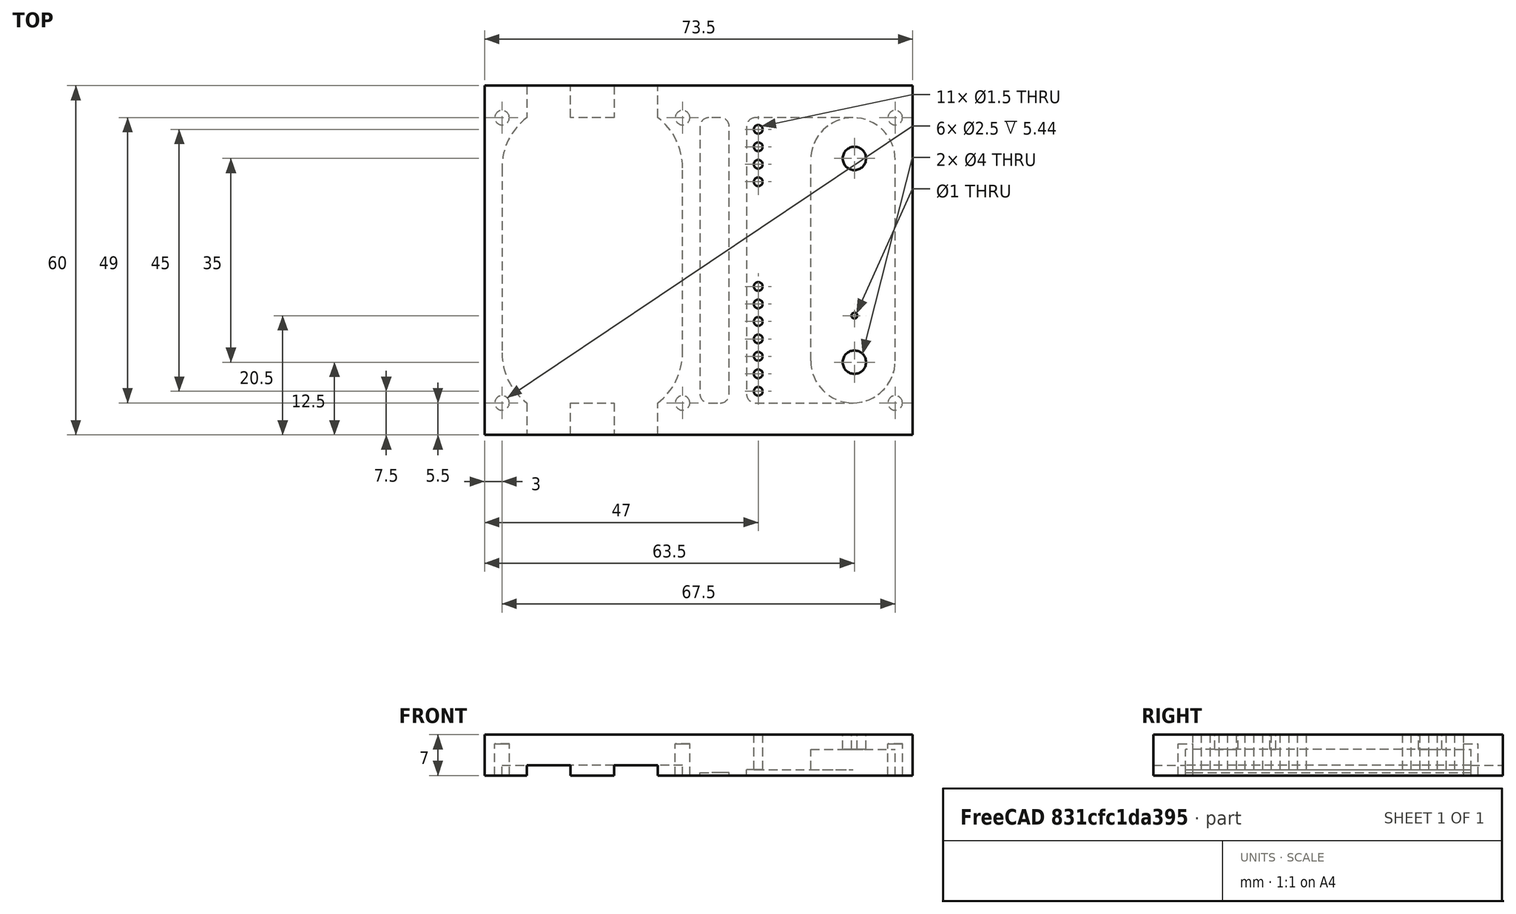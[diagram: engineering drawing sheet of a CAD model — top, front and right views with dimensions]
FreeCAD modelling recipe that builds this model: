
FCSTD DOCUMENT  (FreeCAD 0.20R29177 +426 (Git))
Label: TopCover_2D_TextLaserEngraving
License: All rights reserved
LicenseURL: http://en.wikipedia.org/wiki/All_rights_reserved
objects: Part::Part2DObjectPython×37, Part::Feature×1, App::DocumentObjectGroup×1, App::Part×1
note: 38 computed .brp shape members not serialized (recipe doc carries the construction recipe); baked Part::Feature solids carry a one-line shape summary decoded from their .brp

FEATURE [Part::Feature] Part__Feature001  label="TopCover3D"
  Placement = pos=(0,0,-7.01) rot=(0.707107,-0.707107,0;3.14159rad)
  shape: bbox 73.5 x 60 x 7 mm, 72 faces (baked)
FEATURE [Part::Part2DObjectPython] Shape2DView  label="TopCover_2D"  # Draft 2D object (typed FeaturePython)
  AutoUpdate = true
  Clip = false
  FaceNumbers = [71]
  FuseArch = false
  HiddenLines = false
  InPlace = true
  OnlySolids = false
  Projection = (0,8.74228e-08,-1)
  ProjectionMode = 0
  SegmentLength = 0.05
  Tessellation = false
  VisibleOnly = false
FEATURE [Part::Part2DObjectPython] ShapeString  label="POWER"  # Draft 2D object (typed FeaturePython)
  FontFile = <path>
  MakeFace = true
  Placement = pos=(-25.5,-50.85,0) rot=(0,0,1;0rad)
  Size = 2
  String = POWER
  Tracking = 0
  expr: String = Label
FEATURE [Part::Part2DObjectPython] Shape2DView001  # Draft 2D object (typed FeaturePython)
  AutoUpdate = true
  Base = -> ShapeString
  Clip = false
  FuseArch = false
  HiddenLines = false
  InPlace = true
  OnlySolids = false
  Projection = (0,0,1)
  ProjectionMode = 0
  SegmentLength = 0.05
  Tessellation = false
  VisibleOnly = false
FEATURE [Part::Part2DObjectPython] ShapeString001  label="READY"  # Draft 2D object (typed FeaturePython)
  FontFile = <path>
  MakeFace = true
  Placement = pos=(-25.5,-47.85,0) rot=(0,0,1;0rad)
  Size = 2
  String = READY
  Tracking = 0
  expr: String = Label
FEATURE [Part::Part2DObjectPython] Shape2DView002  # Draft 2D object (typed FeaturePython)
  AutoUpdate = true
  Base = -> ShapeString001
  Clip = false
  FuseArch = false
  HiddenLines = false
  InPlace = true
  OnlySolids = false
  Projection = (0,0,1)
  ProjectionMode = 0
  SegmentLength = 0.05
  Tessellation = false
  VisibleOnly = false
FEATURE [Part::Part2DObjectPython] ShapeString002  label="WAIT"  # Draft 2D object (typed FeaturePython)
  FontFile = <path>
  MakeFace = true
  Placement = pos=(-25.3,-44.85,0) rot=(0,0,1;0rad)
  Size = 2
  String = WAIT
  Tracking = 0
  expr: String = Label
FEATURE [Part::Part2DObjectPython] Shape2DView003  # Draft 2D object (typed FeaturePython)
  AutoUpdate = true
  Base = -> ShapeString002
  Clip = false
  FuseArch = false
  HiddenLines = false
  InPlace = true
  OnlySolids = false
  Projection = (0,0,1)
  ProjectionMode = 0
  SegmentLength = 0.05
  Tessellation = false
  VisibleOnly = false
FEATURE [Part::Part2DObjectPython] ShapeString003  label="PORT1"  # Draft 2D object (typed FeaturePython)
  FontFile = <path>
  MakeFace = true
  Placement = pos=(-25.5,-41.85,0) rot=(0,0,1;0rad)
  Size = 2
  String = PORT1
  Tracking = 0
  expr: String = Label
FEATURE [Part::Part2DObjectPython] Shape2DView004  # Draft 2D object (typed FeaturePython)
  AutoUpdate = true
  Base = -> ShapeString003
  Clip = false
  FuseArch = false
  HiddenLines = false
  InPlace = true
  OnlySolids = false
  Projection = (0,0,1)
  ProjectionMode = 0
  SegmentLength = 0.05
  Tessellation = false
  VisibleOnly = false
FEATURE [Part::Part2DObjectPython] ShapeString004  label="PORT2"  # Draft 2D object (typed FeaturePython)
  FontFile = <path>
  MakeFace = true
  Placement = pos=(-25.5,-38.85,0) rot=(0,0,1;0rad)
  Size = 2
  String = PORT2
  Tracking = 0
  expr: String = Label
FEATURE [Part::Part2DObjectPython] Shape2DView005  # Draft 2D object (typed FeaturePython)
  AutoUpdate = true
  Base = -> ShapeString004
  Clip = false
  FuseArch = false
  HiddenLines = false
  InPlace = true
  OnlySolids = false
  Projection = (0,0,1)
  ProjectionMode = 0
  SegmentLength = 0.05
  Tessellation = false
  VisibleOnly = false
FEATURE [Part::Part2DObjectPython] ShapeString005  label="PORT3"  # Draft 2D object (typed FeaturePython)
  FontFile = <path>
  MakeFace = true
  Placement = pos=(-25.5,-35.85,0) rot=(0,0,1;0rad)
  Size = 2
  String = PORT3
  Tracking = 0
  expr: String = Label
FEATURE [Part::Part2DObjectPython] Shape2DView006  # Draft 2D object (typed FeaturePython)
  AutoUpdate = true
  Base = -> ShapeString005
  Clip = false
  FuseArch = false
  HiddenLines = false
  InPlace = true
  OnlySolids = false
  Projection = (0,0,1)
  ProjectionMode = 0
  SegmentLength = 0.05
  Tessellation = false
  VisibleOnly = false
FEATURE [Part::Part2DObjectPython] ShapeString006  label="PORT4"  # Draft 2D object (typed FeaturePython)
  FontFile = <path>
  MakeFace = true
  Placement = pos=(-25.5,-32.85,0) rot=(0,0,1;0rad)
  Size = 2
  String = PORT4
  Tracking = 0
  expr: String = Label
FEATURE [Part::Part2DObjectPython] Shape2DView007  # Draft 2D object (typed FeaturePython)
  AutoUpdate = true
  Base = -> ShapeString006
  Clip = false
  FuseArch = false
  HiddenLines = false
  InPlace = true
  OnlySolids = false
  Projection = (0,0,1)
  ProjectionMode = 0
  SegmentLength = 0.05
  Tessellation = false
  VisibleOnly = false
FEATURE [Part::Part2DObjectPython] ShapeString007  label="OPEN"  # Draft 2D object (typed FeaturePython)
  FontFile = <path>
  MakeFace = true
  Placement = pos=(-25.5,-14.85,0) rot=(0,0,1;0rad)
  Size = 2
  String = OPEN
  Tracking = 0
  expr: String = Label
FEATURE [Part::Part2DObjectPython] Shape2DView008  # Draft 2D object (typed FeaturePython)
  AutoUpdate = true
  Base = -> ShapeString007
  Clip = false
  FuseArch = false
  HiddenLines = false
  InPlace = true
  OnlySolids = false
  Projection = (0,0,1)
  ProjectionMode = 0
  SegmentLength = 0.05
  Tessellation = false
  VisibleOnly = false
FEATURE [Part::Part2DObjectPython] ShapeString008  label="SHORT"  # Draft 2D object (typed FeaturePython)
  FontFile = <path>
  MakeFace = true
  Placement = pos=(-25.5,-11.85,0) rot=(0,0,1;0rad)
  Size = 2
  String = SHORT
  Tracking = 0
  expr: String = Label
FEATURE [Part::Part2DObjectPython] Shape2DView009  # Draft 2D object (typed FeaturePython)
  AutoUpdate = true
  Base = -> ShapeString008
  Clip = false
  FuseArch = false
  HiddenLines = false
  InPlace = true
  OnlySolids = false
  Projection = (0,0,1)
  ProjectionMode = 0
  SegmentLength = 0.05
  Tessellation = false
  VisibleOnly = false
FEATURE [Part::Part2DObjectPython] ShapeString009  label="LOAD"  # Draft 2D object (typed FeaturePython)
  FontFile = <path>
  MakeFace = true
  Placement = pos=(-25.5,-8.85,0) rot=(0,0,1;0rad)
  Size = 2
  String = LOAD
  Tracking = 0
  expr: String = Label
FEATURE [Part::Part2DObjectPython] Shape2DView010  # Draft 2D object (typed FeaturePython)
  AutoUpdate = true
  Base = -> ShapeString009
  Clip = false
  FuseArch = false
  HiddenLines = false
  InPlace = true
  OnlySolids = false
  Projection = (0,0,1)
  ProjectionMode = 0
  SegmentLength = 0.05
  Tessellation = false
  VisibleOnly = false
FEATURE [Part::Part2DObjectPython] ShapeString010  label="THROUGH"  # Draft 2D object (typed FeaturePython)
  FontFile = <path>
  MakeFace = true
  Placement = pos=(-25.5,-5.85,0) rot=(0,0,1;0rad)
  Size = 2
  String = THROUGH
  Tracking = 0
  expr: String = Label
FEATURE [Part::Part2DObjectPython] Shape2DView011  # Draft 2D object (typed FeaturePython)
  AutoUpdate = true
  Base = -> ShapeString010
  Clip = false
  FuseArch = false
  HiddenLines = false
  InPlace = true
  OnlySolids = false
  Projection = (0,0,1)
  ProjectionMode = 0
  SegmentLength = 0.05
  Tessellation = false
  VisibleOnly = false
FEATURE [Part::Part2DObjectPython] ShapeString011  label="PORT"  # Draft 2D object (typed FeaturePython)
  FontFile = <path>
  MakeFace = true
  Placement = pos=(-5.5,-48,0) rot=(0,0,1;1.5708rad)
  Size = 2
  String = PORT
  Tracking = 0
  expr: String = Label
FEATURE [Part::Part2DObjectPython] Shape2DView012  # Draft 2D object (typed FeaturePython)
  AutoUpdate = true
  Base = -> ShapeString011
  Clip = false
  FuseArch = false
  HiddenLines = false
  InPlace = true
  OnlySolids = false
  Projection = (0,0,1)
  ProjectionMode = 0
  SegmentLength = 0.05
  Tessellation = false
  VisibleOnly = false
FEATURE [Part::Part2DObjectPython] ShapeString012  label="BOOTSEL"  # Draft 2D object (typed FeaturePython)
  FontFile = <path>
  MakeFace = true
  Placement = pos=(-7.75,-39,0) rot=(0,0,1;1.5708rad)
  Size = 1
  String = BOOTSEL
  Tracking = 0
  expr: String = Label
FEATURE [Part::Part2DObjectPython] Shape2DView013  # Draft 2D object (typed FeaturePython)
  AutoUpdate = true
  Base = -> ShapeString012
  Clip = false
  FuseArch = false
  HiddenLines = false
  InPlace = true
  OnlySolids = false
  Projection = (0,0,1)
  ProjectionMode = 0
  SegmentLength = 0.05
  Tessellation = false
  VisibleOnly = false
FEATURE [Part::Part2DObjectPython] ShapeString013  label="FUNCTION"  # Draft 2D object (typed FeaturePython)
  FontFile = <path>
  MakeFace = true
  Placement = pos=(-5.5,-15.5,0) rot=(0,0,1;1.5708rad)
  Size = 2
  String = FUNCTION
  Tracking = 0
  expr: String = Label
FEATURE [Part::Part2DObjectPython] Shape2DView014  # Draft 2D object (typed FeaturePython)
  AutoUpdate = true
  Base = -> ShapeString013
  Clip = false
  FuseArch = false
  HiddenLines = false
  InPlace = true
  OnlySolids = false
  Projection = (0,0,1)
  ProjectionMode = 0
  SegmentLength = 0.05
  Tessellation = false
  VisibleOnly = false
FEATURE [Part::Part2DObjectPython] ShapeString015  label="PORT2_SMA"  # Draft 2D object (typed FeaturePython)
  FontFile = <path>
  MakeFace = true
  Placement = pos=(-61.5,-5.85,0) rot=(0,0,1;1.5708rad)
  Size = 2
  String = PORT2
  Tracking = 0
FEATURE [Part::Part2DObjectPython] Shape2DView015  # Draft 2D object (typed FeaturePython)
  AutoUpdate = true
  Base = -> ShapeString015
  Clip = false
  FuseArch = false
  HiddenLines = false
  InPlace = true
  OnlySolids = false
  Projection = (0,0,1)
  ProjectionMode = 0
  SegmentLength = 0.05
  Tessellation = false
  VisibleOnly = false
FEATURE [Part::Part2DObjectPython] ShapeString014  label="PORT1_SMA"  # Draft 2D object (typed FeaturePython)
  FontFile = <path>
  MakeFace = true
  Placement = pos=(-61.5,-55.9,0) rot=(0,0,1;1.5708rad)
  Size = 2
  String = PORT1
  Tracking = 0
FEATURE [Part::Part2DObjectPython] Shape2DView016  # Draft 2D object (typed FeaturePython)
  AutoUpdate = true
  Base = -> ShapeString014
  Clip = false
  FuseArch = false
  HiddenLines = false
  InPlace = true
  OnlySolids = false
  Projection = (0,0,1)
  ProjectionMode = 0
  SegmentLength = 0.05
  Tessellation = false
  VisibleOnly = false
FEATURE [Part::Part2DObjectPython] ShapeString017  label="PORT4_SMA"  # Draft 2D object (typed FeaturePython)
  FontFile = <path>
  MakeFace = true
  Placement = pos=(-45.5,-5.85,0) rot=(0,0,1;1.5708rad)
  Size = 2
  String = PORT4
  Tracking = 0
FEATURE [Part::Part2DObjectPython] Shape2DView017  # Draft 2D object (typed FeaturePython)
  AutoUpdate = true
  Base = -> ShapeString017
  Clip = false
  FuseArch = false
  HiddenLines = false
  InPlace = true
  OnlySolids = false
  Projection = (0,0,1)
  ProjectionMode = 0
  SegmentLength = 0.05
  Tessellation = false
  VisibleOnly = false
FEATURE [Part::Part2DObjectPython] ShapeString016  label="PORT3_SMA"  # Draft 2D object (typed FeaturePython)
  FontFile = <path>
  MakeFace = true
  Placement = pos=(-45.5,-55.85,0) rot=(0,0,1;1.5708rad)
  Size = 2
  String = PORT3
  Tracking = 0
FEATURE [App::DocumentObjectGroup] Group  label="DraftText"
  Group = -> [ShapeString,ShapeString001,ShapeString002,ShapeString003,ShapeString004,ShapeString005,ShapeString006,ShapeString007,ShapeString008,ShapeString009,ShapeString010,ShapeString011,ShapeString012,ShapeString013,ShapeString015,ShapeString014,ShapeString017,ShapeString016]
FEATURE [Part::Part2DObjectPython] Shape2DView018  # Draft 2D object (typed FeaturePython)
  AutoUpdate = true
  Base = -> ShapeString016
  Clip = false
  FuseArch = false
  HiddenLines = false
  InPlace = true
  OnlySolids = false
  Projection = (0,0,1)
  ProjectionMode = 0
  SegmentLength = 0.05
  Tessellation = false
  VisibleOnly = false
FEATURE [App::Part] Part
  Group = -> [Shape2DView,ShapeString,Shape2DView001,ShapeString001,Shape2DView002,ShapeString002,Shape2DView003,ShapeString003,Shape2DView004,ShapeString004,Shape2DView005,ShapeString005,Shape2DView006,ShapeString006,Shape2DView007,ShapeString007,Shape2DView008,ShapeString008,Shape2DView009,ShapeString009,Shape2DView010,ShapeString010,Shape2DView011,ShapeString011,Shape2DView012,ShapeString012,Shape2DView013,+10 more]
  Origin = -> Origin
note: 18 file-system paths scrubbed to <path> (originals preserved in the JSON sidecar)
